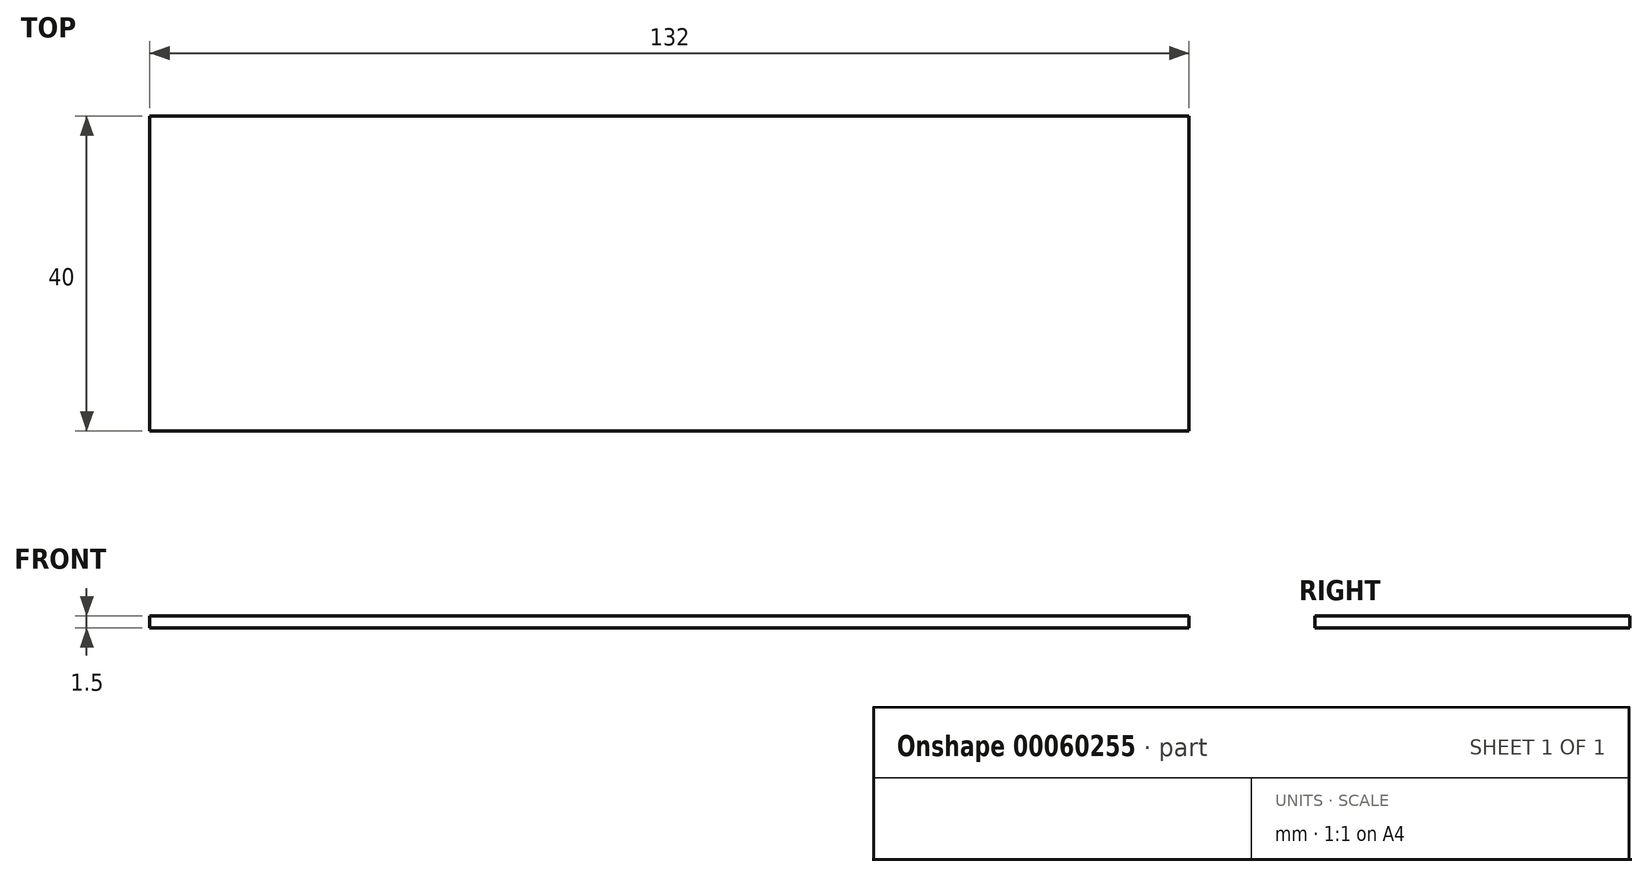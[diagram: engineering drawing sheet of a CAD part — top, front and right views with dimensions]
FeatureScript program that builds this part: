
annotation { "Feature Type Name" : "Feature", "Feature Type Description" : "" }
export const myFeature = defineFeature(function(context is Context, id is Id, definition is map)
    precondition{}
    {
        {
            var Q0;
            Q0=qCreatedBy(makeId("Top.planeOp"),FACE);
            var sketch = newSketch(context, id + "F0", { "sketchPlane" : qUnion([Q0])});
            skLineSegment(sketch, "E0.bottom", {"start": v(0, 0) * mm, "end": v(132, 0) * mm});
            skLineSegment(sketch, "E0.top", {"start": v(0, -40) * mm, "end": v(132, -40) * mm});
            skLineSegment(sketch, "E0.left", {"start": v(0, 0) * mm, "end": v(0, -40) * mm});
            skLineSegment(sketch, "E0.right", {"start": v(132, 0) * mm, "end": v(132, -40) * mm});
            skSolve(sketch);
        }
        {
            var Q0;
            Q0 = qSketchRegion(id + "F0", true);
            extrude(context, id + "F1", {"entities" : qUnion([Q0]), "depth" : 1.5 * mm});
        }
    });
